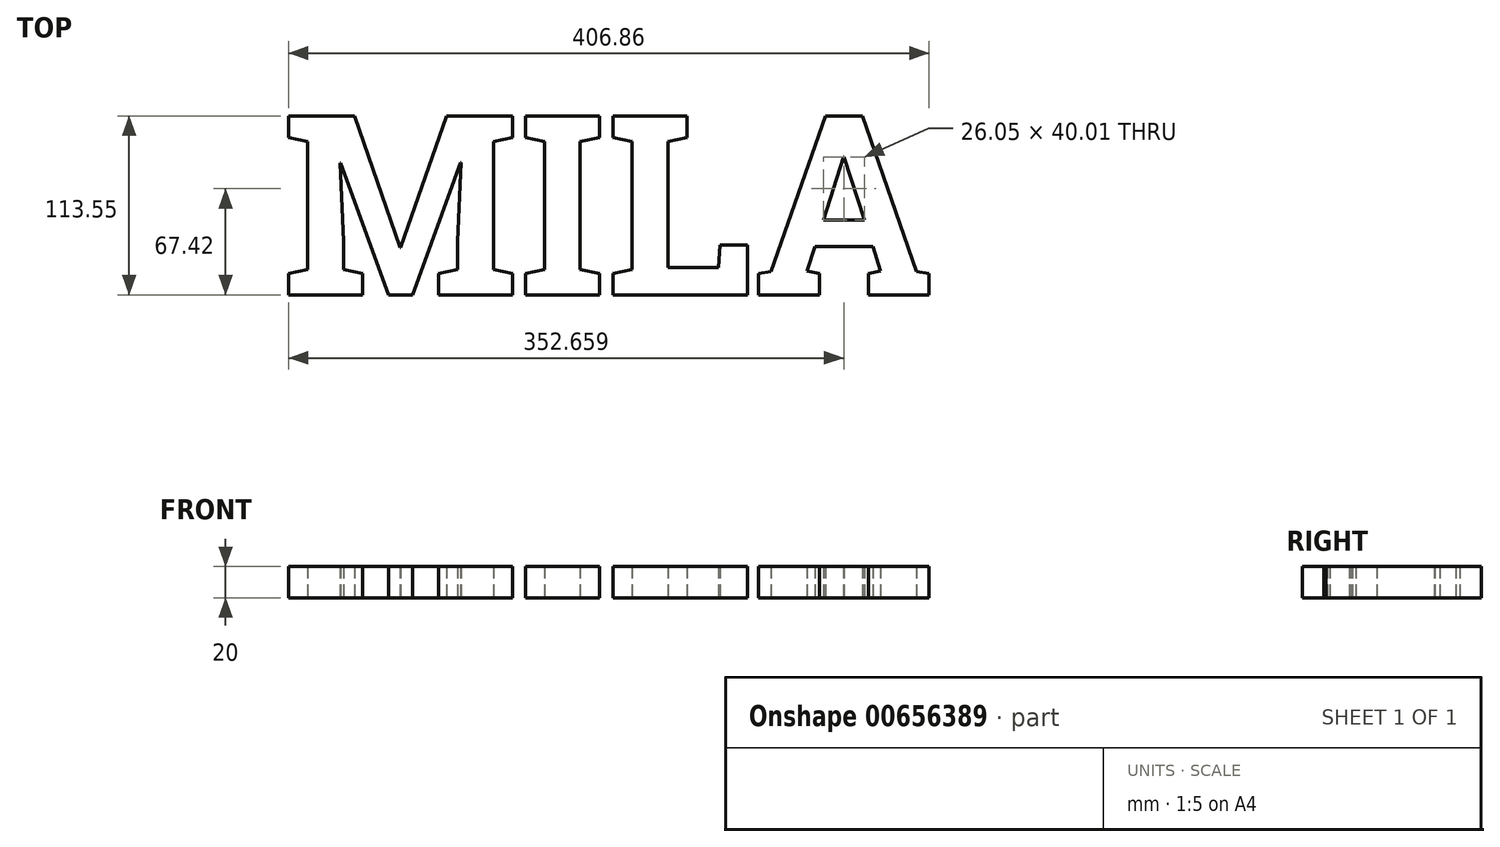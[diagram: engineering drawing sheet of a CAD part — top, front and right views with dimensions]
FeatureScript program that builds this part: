
annotation { "Feature Type Name" : "Feature", "Feature Type Description" : "" }
export const myFeature = defineFeature(function(context is Context, id is Id, definition is map)
    precondition{}
    {
        {
            var Q0;
            Q0=qCreatedBy(makeId("Top.planeOp"),FACE);
            var sketch = newSketch(context, id + "F0", { "sketchPlane" : qUnion([Q0])});
            skText(sketch, "E0", { "text": "MILA\n", "fontName": "RobotoSlab-Bold.ttf"});
            const initialGuessF0  = {"E0": [-0.2105, 0, 1, 0, 0.115]};
            skSetInitialGuess(sketch, initialGuessF0);
            skSolve(sketch);
        }
        {
            var Q0;
            Q0 = qSketchRegion(id + "F0", true);
            extrude(context, id + "F1", {"entities" : qUnion([Q0]), "depth" : 20 * mm, "offsetDistance" : 25 * mm});
        }
    });
